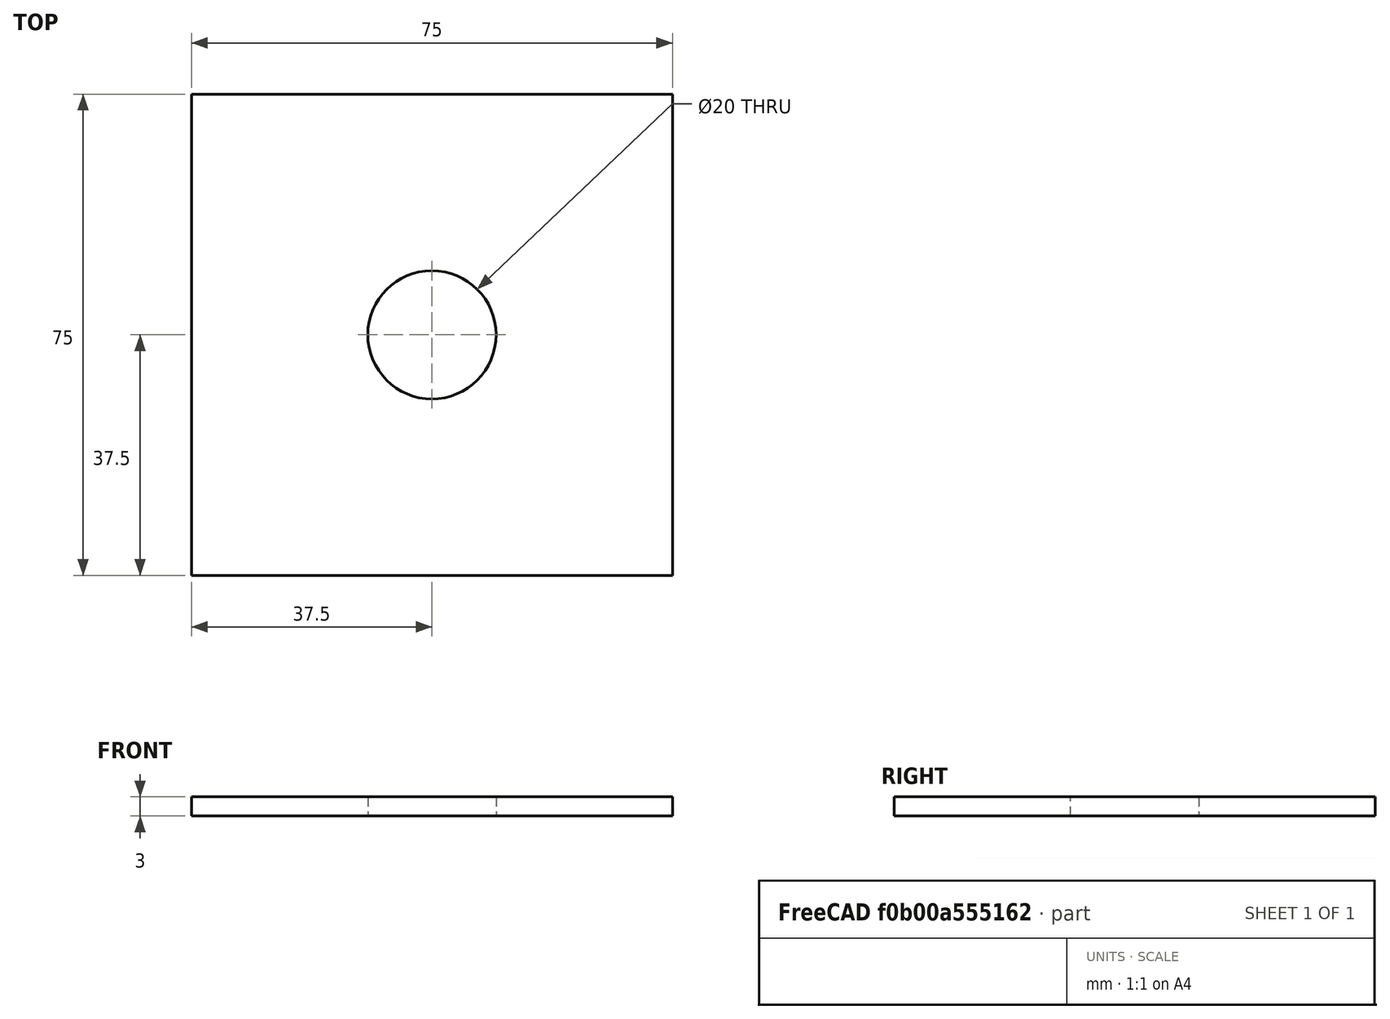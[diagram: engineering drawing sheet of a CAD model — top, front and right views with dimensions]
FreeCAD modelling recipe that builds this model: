
FCSTD DOCUMENT  (FreeCAD 0.20R29603 (Git))
Label: Platte_mitloch
License: All rights reserved
LicenseURL: http://en.wikipedia.org/wiki/All_rights_reserved
objects: TechDraw::DrawViewDimension×4, TechDraw::DrawViewPart×3, PartDesign::AdditiveBox×1, PartDesign::SubtractiveCylinder×1, PartDesign::Body×1, TechDraw::DrawSVGTemplate×1, TechDraw::DrawPage×1
note: 5 computed .brp shape members not serialized (recipe doc carries the construction recipe); baked Part::Feature solids carry a one-line shape summary decoded from their .brp

FEATURE [PartDesign::AdditiveBox] Box
  AttacherType = Attacher::AttachEngine3D
  Height = 3
  Length = 75
  Width = 75
FEATURE [PartDesign::SubtractiveCylinder] Cylinder
  Angle = 360
  AttacherType = Attacher::AttachEngine3D
  AttachmentOffset = pos=(-37.5,0,-3) rot=(0,0,1;0rad)
  BaseFeature = -> Box
  FirstAngle = 0
  Height = 3
  MapMode = 5
  Placement = pos=(37.5,37.5,-4e-15) rot=(0,0,-1;1.5708rad)
  Radius = 10
  SecondAngle = 0
FEATURE [PartDesign::Body] Body
  Group = -> [Box,Cylinder]
  Origin = -> Origin
  Tip = -> Cylinder
FEATURE [TechDraw::DrawSVGTemplate] Template
  EditableTexts = Designed_by_Name=B. Schulze; Drawing_number=1; FC-Date=03.08.2023; FC-SC=1:1; FC-SH=4; FC-Title=Eisdosierer; Subtitle=Seitententeile Dosierer; Weight=0
  Height = 210
  Orientation = 1
  Width = 297
FEATURE [TechDraw::DrawViewPart] View  label="Rechts"
  Caption = Rechts
  CoarseView = false
  Direction = (0,0,1)
  Focus = 100
  HardHidden = false
  IsoCount = 0
  IsoHidden = false
  IsoVisible = false
  LockPosition = false
  Perspective = false
  Rotation = 0
  ScaleType = 0
  SeamHidden = false
  SeamVisible = true
  SmoothHidden = false
  SmoothVisible = true
  Source = -> [Body]
  X = 123.857
  XDirection = (1,0,0)
  Y = 145.179
FEATURE [TechDraw::DrawViewPart] View001  label="Links"
  Caption = Links
  CoarseView = false
  Direction = (0,0,1)
  Focus = 100
  HardHidden = false
  IsoCount = 0
  IsoHidden = false
  IsoVisible = false
  LockPosition = false
  Perspective = false
  Rotation = 0
  ScaleType = 0
  SeamHidden = false
  SeamVisible = true
  SmoothHidden = false
  SmoothVisible = true
  Source = -> [Box]
  X = 237.92
  XDirection = (1,0,0)
  Y = 144.643
FEATURE [TechDraw::DrawViewPart] View002  label="Seite"
  Caption = Seite
  CoarseView = false
  Direction = (1,0,0)
  Focus = 100
  HardHidden = false
  IsoCount = 0
  IsoHidden = false
  IsoVisible = false
  LockPosition = false
  Perspective = false
  Rotation = 0
  ScaleType = 0
  SeamHidden = false
  SeamVisible = true
  SmoothHidden = false
  SmoothVisible = true
  Source = -> [Cylinder]
  X = 43.773
  XDirection = (0,0,-1)
  Y = 140.316
FEATURE [TechDraw::DrawViewDimension] Dimension
  AngleOverride = false
  Arbitrary = false
  ArbitraryTolerances = false
  EqualTolerance = true
  ExtensionAngle = 0
  FormatSpec = %.2w
  FormatSpecOverTolerance = %+.2w
  FormatSpecUnderTolerance = %+.2w
  Inverted = false
  LineAngle = 0
  LockPosition = false
  MeasureType = 1
  OverTolerance = 0
  References2D = -> [View002]
  Rotation = 0
  ScaleType = 0
  TheoreticalExact = false
  Type = 1
  UnderTolerance = 0
  X = 9.14426
  Y = -31.1785
FEATURE [TechDraw::DrawViewDimension] Dimension001
  AngleOverride = false
  Arbitrary = false
  ArbitraryTolerances = false
  EqualTolerance = true
  ExtensionAngle = 0
  FormatSpec = %.2w
  FormatSpecOverTolerance = %+.2w
  FormatSpecUnderTolerance = %+.2w
  Inverted = false
  LineAngle = 0
  LockPosition = false
  MeasureType = 1
  OverTolerance = 0
  References2D = -> [View]
  Rotation = 0
  ScaleType = 0
  TheoreticalExact = false
  Type = 2
  UnderTolerance = 0
  X = -49.4048
  Y = 2.12798
FEATURE [TechDraw::DrawViewDimension] Dimension002
  AngleOverride = false
  Arbitrary = false
  ArbitraryTolerances = false
  EqualTolerance = true
  ExtensionAngle = 0
  FormatSpec = %.2w
  FormatSpecOverTolerance = %+.2w
  FormatSpecUnderTolerance = %+.2w
  Inverted = false
  LineAngle = 0
  LockPosition = false
  MeasureType = 1
  OverTolerance = 0
  References2D = -> [View]
  Rotation = 0
  ScaleType = 0
  TheoreticalExact = false
  Type = 1
  UnderTolerance = 0
  X = -0.372024
  Y = 49.3006
FEATURE [TechDraw::DrawViewDimension] Dimension003
  AngleOverride = false
  Arbitrary = false
  ArbitraryTolerances = false
  EqualTolerance = true
  ExtensionAngle = 0
  FormatSpec = ⌀%.2w
  FormatSpecOverTolerance = %+.2w
  FormatSpecUnderTolerance = %+.2w
  Inverted = false
  LineAngle = 0
  LockPosition = false
  MeasureType = 1
  OverTolerance = 0
  References2D = -> [View]
  Rotation = 0
  ScaleType = 0
  TheoreticalExact = false
  Type = 5
  UnderTolerance = 0
  X = -1.86012
  Y = 5.20833
FEATURE [TechDraw::DrawPage] Page
  KeepUpdated = true
  NextBalloonIndex = 1
  ProjectionType = 0
  Template = -> Template
  Views = -> [View,View001,View002,Dimension,Dimension001,Dimension002,Dimension003]
